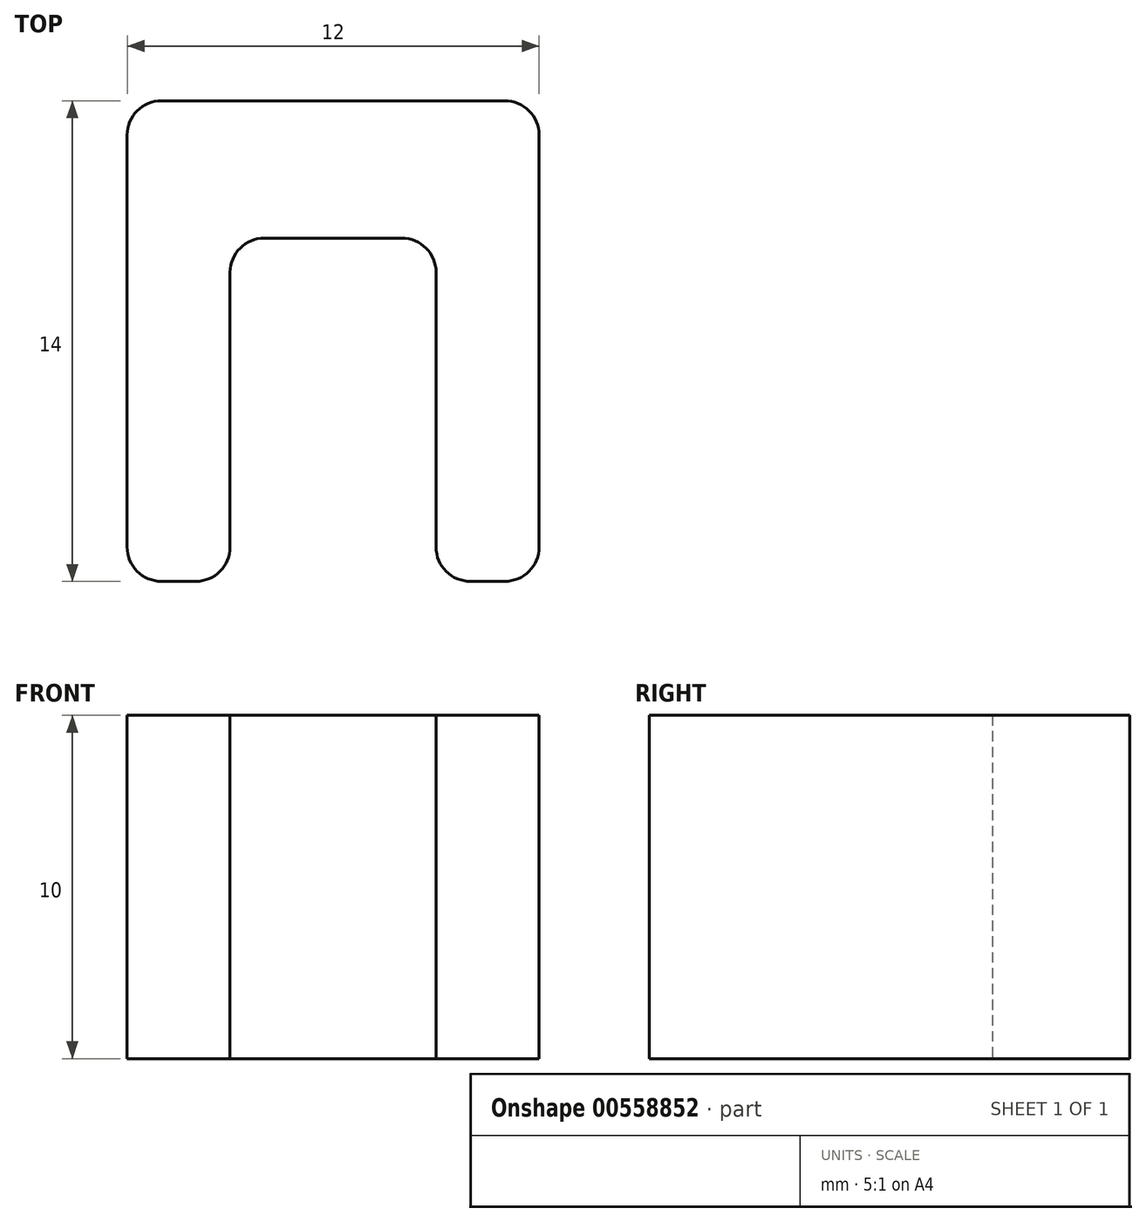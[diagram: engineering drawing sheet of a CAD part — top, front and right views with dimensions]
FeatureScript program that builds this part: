
annotation { "Feature Type Name" : "Feature", "Feature Type Description" : "" }
export const myFeature = defineFeature(function(context is Context, id is Id, definition is map)
    precondition{}
    {
        {
            var Q0;
            Q0=qCreatedBy(makeId("Top.planeOp"),FACE);
            var sketch = newSketch(context, id + "F0", { "sketchPlane" : qUnion([Q0])});
            skLineSegment(sketch, "E0.top", {"start": v(-46.02, 20.48) * mm, "end": v(-42.02, 20.48) * mm});
            skLineSegment(sketch, "E0.left", {"start": v(-47.02, 11.48) * mm, "end": v(-47.02, 19.48) * mm});
            skLineSegment(sketch, "E0.right", {"start": v(-41.02, 11.48) * mm, "end": v(-41.02, 19.48) * mm});
            skLineSegment(sketch, "E1.bottom", {"start": v(-49.02, 10.48) * mm, "end": v(-48.02, 10.48) * mm});
            skLineSegment(sketch, "E1.top", {"start": v(-49.02, 24.48) * mm, "end": v(-39.02, 24.48) * mm});
            skLineSegment(sketch, "E1.left", {"start": v(-50.02, 11.48) * mm, "end": v(-50.02, 23.48) * mm});
            skLineSegment(sketch, "E1.right", {"start": v(-38.02, 11.48) * mm, "end": v(-38.02, 23.48) * mm});
            skPoint(sketch, "E2.visualSharp", {"position": v(-50.02, 24.48) * mm});
            skArc(sketch, "E2.filletArc", {"start": v(-49.02, 24.48) * mm, "mid": v(-49.73, 24.19) * mm, "end": v(-50.02, 23.48) * mm});
            skPoint(sketch, "E3.visualSharp", {"position": v(-47.02, 20.48) * mm});
            skArc(sketch, "E3.filletArc", {"start": v(-46.02, 20.48) * mm, "mid": v(-46.73, 20.19) * mm, "end": v(-47.02, 19.48) * mm});
            skPoint(sketch, "E4.visualSharp", {"position": v(-41.02, 20.48) * mm});
            skArc(sketch, "E4.filletArc", {"start": v(-41.02, 19.48) * mm, "mid": v(-41.32, 20.19) * mm, "end": v(-42.02, 20.48) * mm});
            skPoint(sketch, "E5.visualSharp", {"position": v(-38.02, 24.48) * mm});
            skArc(sketch, "E5.filletArc", {"start": v(-38.02, 23.48) * mm, "mid": v(-38.32, 24.19) * mm, "end": v(-39.02, 24.48) * mm});
            skPoint(sketch, "E6.visualSharp", {"position": v(-38.02, 10.48) * mm});
            skArc(sketch, "E6.filletArc", {"start": v(-39.02, 10.48) * mm, "mid": v(-38.32, 10.77) * mm, "end": v(-38.02, 11.48) * mm});
            skPoint(sketch, "E7.visualSharp", {"position": v(-41.02, 10.48) * mm});
            skPoint(sketch, "E8.visualSharp", {"position": v(-47.02, 10.48) * mm});
            skPoint(sketch, "E9.visualSharp", {"position": v(-50.02, 10.48) * mm});
            skArc(sketch, "E9.filletArc", {"start": v(-50.02, 11.48) * mm, "mid": v(-49.73, 10.77) * mm, "end": v(-49.02, 10.48) * mm});
            skLineSegment(sketch, "E10.trimOffspring", {"start": v(-40.02, 10.48) * mm, "end": v(-39.02, 10.48) * mm});
            skLineSegment(sketch, "E11", {"start": v(-47.02, 11.48) * mm, "end": v(-47.02, 11.48) * mm});
            skLineSegment(sketch, "E12", {"start": v(-41.02, 11.48) * mm, "end": v(-41.02, 11.48) * mm});
            skArc(sketch, "E13.filletArc", {"start": v(-48.02, 10.48) * mm, "mid": v(-47.32, 10.77) * mm, "end": v(-47.02, 11.48) * mm});
            skArc(sketch, "E14.filletArc", {"start": v(-41.02, 11.48) * mm, "mid": v(-40.73, 10.77) * mm, "end": v(-40.02, 10.48) * mm});
            skSolve(sketch);
        }
        {
            var Q0;
            Q0 = qSketchRegion(id + "F0", true);
            extrude(context, id + "F1", {"entities" : qUnion([Q0]), "depth" : 10 * mm, "offsetDistance" : 25 * mm});
        }
    });
